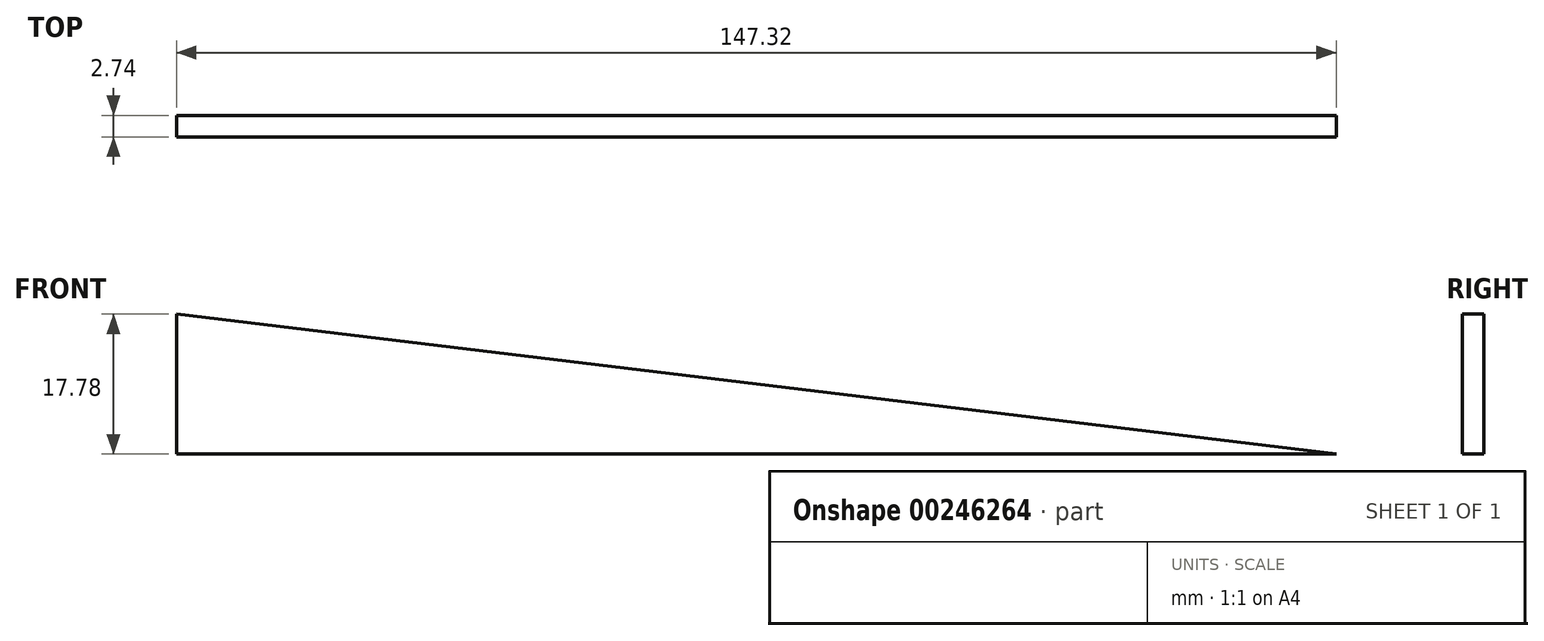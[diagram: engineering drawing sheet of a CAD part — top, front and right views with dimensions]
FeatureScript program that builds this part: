
annotation { "Feature Type Name" : "Feature", "Feature Type Description" : "" }
export const myFeature = defineFeature(function(context is Context, id is Id, definition is map)
    precondition{}
    {
        {
            var Q0;
            Q0=qCreatedBy(makeId("Front.planeOp"),FACE);
            var sketch = newSketch(context, id + "F0", { "sketchPlane" : qUnion([Q0])});
            skLineSegment(sketch, "E0.bottom", {"start": v(-42.82, 24.74) * mm, "end": v(104.5, 24.74) * mm});
            skLineSegment(sketch, "E0.top", {"start": v(-42.82, 6.96) * mm, "end": v(104.5, 6.96) * mm});
            skLineSegment(sketch, "E0.left", {"start": v(-42.82, 24.74) * mm, "end": v(-42.82, 6.96) * mm});
            skLineSegment(sketch, "E0.right", {"start": v(104.5, 24.74) * mm, "end": v(104.5, 6.96) * mm});
            skLineSegment(sketch, "E1", {"start": v(-42.82, 24.74) * mm, "end": v(104.5, 6.96) * mm});
            skSolve(sketch);
        }
        {
            var Q0;
            Q0=makeQuery(id+"F0.imprint","IMPRINT",FACE,{"disambiguationData":[TD([[makeQuery(id+"F0.imprint","IMPRINT",EDGE,{"derivedFrom":sQuery(id+"F0.wireOp",EDGE,"E0.top")}),1.0]])]});
            extrude(context, id + "F1", {"entities" : qUnion([Q0]), "depth" : 2.74 * mm});
        }
    });
